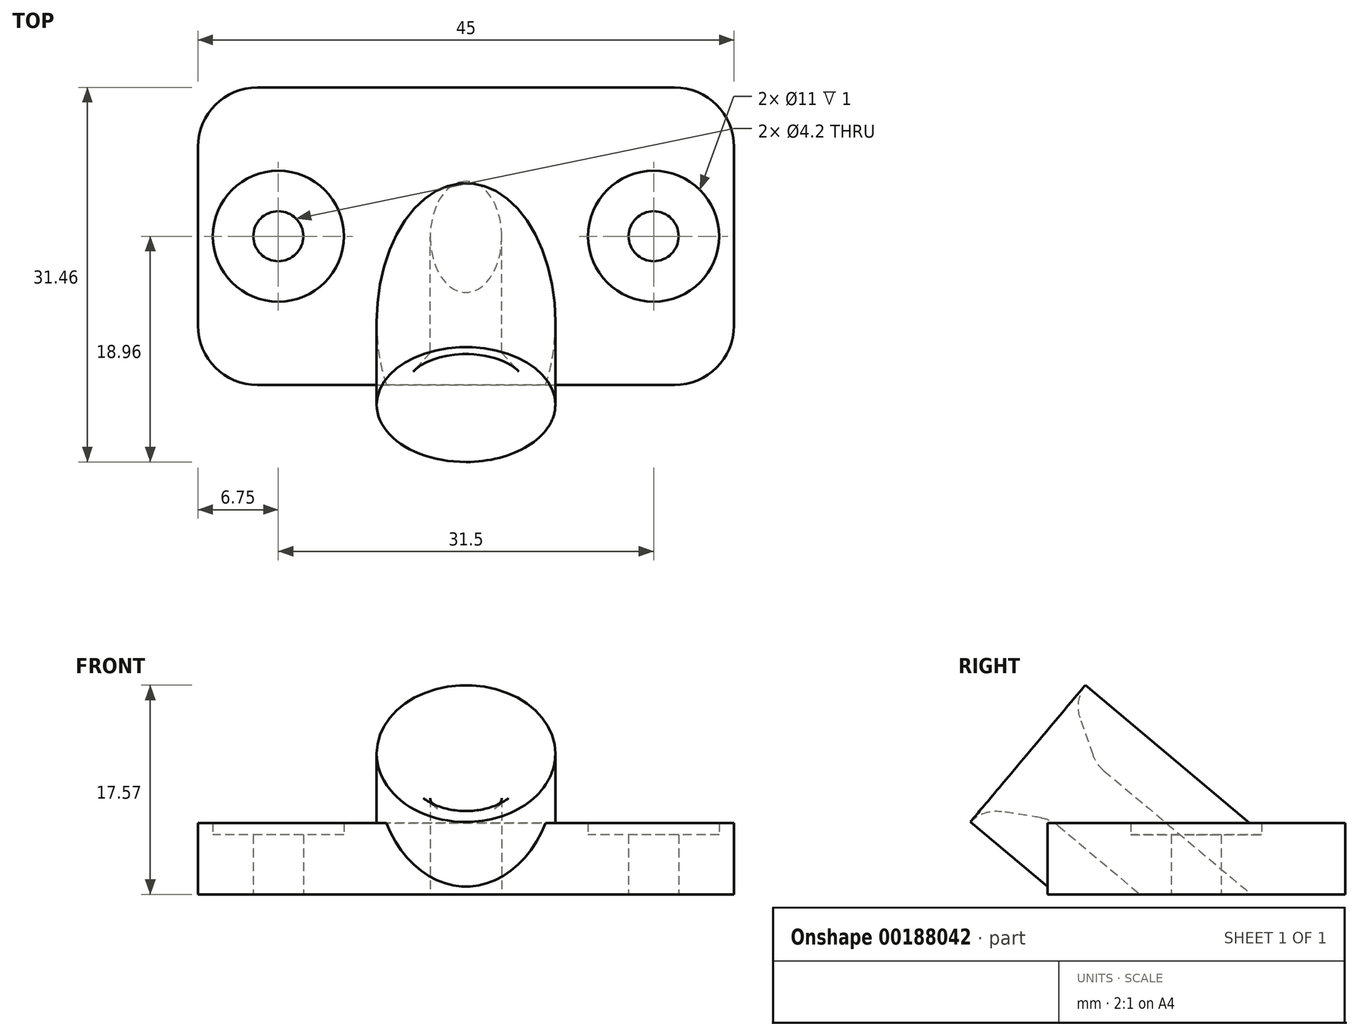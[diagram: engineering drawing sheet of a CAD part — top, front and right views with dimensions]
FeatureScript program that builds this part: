
annotation { "Feature Type Name" : "Feature", "Feature Type Description" : "" }
export const myFeature = defineFeature(function(context is Context, id is Id, definition is map)
    precondition{}
    {
        {
            var Q0;
            Q0=qCreatedBy(makeId("Top.planeOp"),FACE);
            var sketch = newSketch(context, id + "F0", { "sketchPlane" : qUnion([Q0])});
            skLineSegment(sketch, "E0.bottom", {"start": v(0, 0) * mm, "end": v(45, 0) * mm});
            skLineSegment(sketch, "E0.top", {"start": v(0, 25) * mm, "end": v(45, 25) * mm});
            skLineSegment(sketch, "E0.left", {"start": v(0, 0) * mm, "end": v(0, 25) * mm});
            skLineSegment(sketch, "E0.right", {"start": v(45, 0) * mm, "end": v(45, 25) * mm});
            skSolve(sketch);
        }
        {
            var Q0;
            Q0=makeQuery(id+"F0.imprint","IMPRINT",FACE,{"disambiguationData":[TD([[makeQuery(id+"F0.imprint","IMPRINT",EDGE,{"derivedFrom":sQuery(id+"F0.wireOp",EDGE,"E0.bottom")}),1.0]])]});
            extrude(context, id + "F1", {"entities" : qUnion([Q0]), "depth" : 6 * mm});
        }
        {
            var Q0;
            Q0=makeQuery(id+"F1.opExtrude","SWEPT_EDGE",EDGE,{"disambiguationData":[OSD([sQuery(id+"F0.wireOp",EDGE,"E0.top"),sQuery(id+"F0.wireOp",EDGE,"E0.right")])]});
            var Q1;
            Q1=makeQuery(id+"F1.opExtrude","SWEPT_EDGE",EDGE,{"disambiguationData":[OSD([sQuery(id+"F0.wireOp",EDGE,"E0.bottom"),sQuery(id+"F0.wireOp",EDGE,"E0.right")])]});
            var Q2;
            Q2=makeQuery(id+"F1.opExtrude","SWEPT_EDGE",EDGE,{"disambiguationData":[OSD([sQuery(id+"F0.wireOp",EDGE,"E0.top"),sQuery(id+"F0.wireOp",EDGE,"E0.left")])]});
            var Q3;
            Q3=makeQuery(id+"F1.opExtrude","SWEPT_EDGE",EDGE,{"disambiguationData":[OSD([sQuery(id+"F0.wireOp",EDGE,"E0.bottom"),sQuery(id+"F0.wireOp",EDGE,"E0.left")])]});
            fillet(context, id + "F2", {"entities" : qUnion([Q0, Q1, Q2, Q3]), "radius" : 5 * mm, "tangentPropagation" : true, "allowEdgeOverflow" : false});
        }
        {
            var Q0;
            Q0=qCreatedBy(makeId("Top.planeOp"),FACE);
            cPlane(context, id + "F3", {"entities" : qUnion([Q0]), "cplaneType" : CPlaneType.OFFSET, "offset" : 5 * mm, "width" : 150 * mm, "height" : 150 * mm});
        }
        {
            var Q0;
            Q0=qCreatedBy(id+"F3.planeOp",FACE);
            var sketch = newSketch(context, id + "F4", { "sketchPlane" : qUnion([Q0])});
            skCircle(sketch, "E1", {"center": v(6.75, 12.5) * mm, "radius": 5.5 * mm});
            skCircle(sketch, "E2", {"center": v(38.25, 12.5) * mm, "radius": 5.5 * mm});
            skSolve(sketch);
        }
        {
            var Q0;
            Q0=qSketchRegion(id+"F4",true);
            extrude(context, id + "F5", {"entities" : qUnion([Q0]), "operationType" : NewBodyOperationType.REMOVE, "depth" : 25 * mm});
        }
        {
            var Q0;
            Q0=qCreatedBy(makeId("Top.planeOp"),FACE);
            var sketch = newSketch(context, id + "F6", { "sketchPlane" : qUnion([Q0])});
            skCircle(sketch, "E3", {"center": v(6.75, 12.5) * mm, "radius": 2.1 * mm});
            skCircle(sketch, "E4", {"center": v(38.25, 12.5) * mm, "radius": 2.1 * mm});
            skSolve(sketch);
        }
        {
            var Q0;
            Q0=qSketchRegion(id+"F6",true);
            extrude(context, id + "F7", {"entities" : qUnion([Q0]), "operationType" : NewBodyOperationType.REMOVE, "depth" : 25 * mm});
        }
        {
            var Q0;
            Q0=makeQuery(id+"F1.opExtrude","CAP_EDGE",EDGE,{"disambiguationData":[OSD([sQuery(id+"F0.wireOp",EDGE,"E0.bottom")])],"isStart":false});
            cPlane(context, id + "F8", {"entities" : qUnion([Q0]), "cplaneType" : CPlaneType.LINE_ANGLE, "offset" : 25 * mm, "angle" : 140 * degree, "width" : 150 * mm, "height" : 150 * mm});
        }
        {
            var Q0;
            Q0=qCreatedBy(id+"F8.planeOp",FACE);
            var sketch = newSketch(context, id + "F9", { "sketchPlane" : qUnion([Q0])});
            skCircle(sketch, "E5", {"center": v(22.5, 8) * mm, "radius": 7.5 * mm});
            skSolve(sketch);
        }
        {
            var Q0;
            Q0=qSketchRegion(id+"F9",true);
            extrude(context, id + "F10", {"entities" : qUnion([Q0]), "operationType" : NewBodyOperationType.ADD, "depth" : 5 * mm, "hasSecondDirection" : true, "secondDirectionOppositeDirection" : true, "secondDirectionDepth" : 25 * mm});
        }
        {
            var Q0;
            Q0=qCreatedBy(makeId("Top.planeOp"),FACE);
            var sketch = newSketch(context, id + "F11", { "sketchPlane" : qUnion([Q0])});
            skLineSegment(sketch, "E6.bottom", {"start": v(-1.96, -1.35) * mm, "end": v(47.32, -1.35) * mm});
            skLineSegment(sketch, "E6.top", {"start": v(-1.96, 28.88) * mm, "end": v(47.32, 28.88) * mm});
            skLineSegment(sketch, "E6.left", {"start": v(-1.96, -1.35) * mm, "end": v(-1.96, 28.88) * mm});
            skLineSegment(sketch, "E6.right", {"start": v(47.32, -1.35) * mm, "end": v(47.32, 28.88) * mm});
            skSolve(sketch);
        }
        {
            var Q0;
            Q0=qSketchRegion(id+"F11",true);
            extrude(context, id + "F12", {"entities" : qUnion([Q0]), "operationType" : NewBodyOperationType.REMOVE, "oppositeDirection" : true, "depth" : 25 * mm});
        }
        {
            var Q0;
            Q0=makeQuery(id+"F1.opExtrude","SWEPT_FACE",FACE,{"disambiguationData":[OSD([sQuery(id+"F0.wireOp",EDGE,"E0.top")])]});
            var sketch = newSketch(context, id + "F13", { "sketchPlane" : qUnion([Q0])});
            skLineSegment(sketch, "E7.bottom", {"start": v(-3.87, 7.72) * mm, "end": v(-41.53, 7.72) * mm});
            skLineSegment(sketch, "E7.top", {"start": v(-3.87, -2.98) * mm, "end": v(-41.53, -2.98) * mm});
            skLineSegment(sketch, "E7.left", {"start": v(-3.87, 7.72) * mm, "end": v(-3.87, -2.98) * mm});
            skLineSegment(sketch, "E7.right", {"start": v(-41.53, 7.72) * mm, "end": v(-41.53, -2.98) * mm});
            skSolve(sketch);
        }
        {
            var Q0;
            Q0=qSketchRegion(id+"F13",true);
            extrude(context, id + "F14", {"entities" : qUnion([Q0]), "operationType" : NewBodyOperationType.REMOVE, "depth" : 25 * mm});
        }
        {
            var Q0;
            Q0=qCreatedBy(id+"F8.planeOp",FACE);
            var sketch = newSketch(context, id + "F15", { "sketchPlane" : qUnion([Q0])});
            skCircle(sketch, "E8", {"center": v(22.5, 8) * mm, "radius": 3 * mm});
            skSolve(sketch);
        }
        {
            var Q0;
            Q0=qSketchRegion(id+"F15",true);
            extrude(context, id + "F16", {"entities" : qUnion([Q0]), "operationType" : NewBodyOperationType.REMOVE, "depth" : 25 * mm, "hasSecondDirection" : true, "secondDirectionOppositeDirection" : true, "secondDirectionDepth" : 25 * mm});
        }
        {
            var Q0;
            Q0=makeQuery(id+"F16.boolean.opBoolean","INTERSECT",EDGE,{"derivedFrom":[makeQuery(id+"F10.opExtrude","CAP_FACE",FACE,{"disambiguationData":[OSD([sQuery(id+"F9.wireOp",EDGE,"E5")])],"isStart":false}),makeQuery(id+"F16.opExtrude","SWEPT_FACE",FACE,{"disambiguationData":[OSD([sQuery(id+"F15.wireOp",EDGE,"E8")])]})]});
            chamfer(context, id + "F17", {"entities" : qUnion([Q0]), "chamferType" : ChamferType.TWO_OFFSETS, "width1" : 3 * mm, "oppositeDirection" : false, "width2" : 5 * mm, "tangentPropagation" : true});
        }
        {
            var Q0;
            {var subQ0=makeQuery(id+"F16.opExtrude","SWEPT_FACE",FACE,{"disambiguationData":[OSD([sQuery(id+"F15.wireOp",EDGE,"E8")])]});Q0=makeQuery(id+"F17.opChamfer","BLEND_EDGE",EDGE,{"blendedFrom":[makeQuery(id+"F16.boolean.opBoolean","INTERSECT",EDGE,{"derivedFrom":[makeQuery(id+"F10.opExtrude","CAP_FACE",FACE,{"disambiguationData":[OSD([sQuery(id+"F9.wireOp",EDGE,"E5")])],"isStart":false}),subQ0]}),makeQuery(id+"F16.boolean.opBoolean","COPY",FACE,{"derivedFrom":subQ0})],"blendedInto":[makeQuery(id+"F16.boolean.opBoolean","COPY",FACE,{"derivedFrom":subQ0})]});}
            fillet(context, id + "F18", {"entities" : qUnion([Q0]), "radius" : 3 * mm, "tangentPropagation" : true, "allowEdgeOverflow" : false});
        }
        {
            var Q0;
            {var subQ0=makeQuery(id+"F10.opExtrude","CAP_FACE",FACE,{"disambiguationData":[OSD([sQuery(id+"F9.wireOp",EDGE,"E5")])],"isStart":false});Q0=makeQuery(id+"F17.opChamfer","BLEND_EDGE",EDGE,{"blendedFrom":[makeQuery(id+"F16.boolean.opBoolean","INTERSECT",EDGE,{"derivedFrom":[subQ0,makeQuery(id+"F16.opExtrude","SWEPT_FACE",FACE,{"disambiguationData":[OSD([sQuery(id+"F15.wireOp",EDGE,"E8")])]})]}),subQ0],"blendedInto":[subQ0]});}
            fillet(context, id + "F19", {"entities" : qUnion([Q0]), "radius" : 3 * mm, "tangentPropagation" : true, "allowEdgeOverflow" : false});
        }
    });
